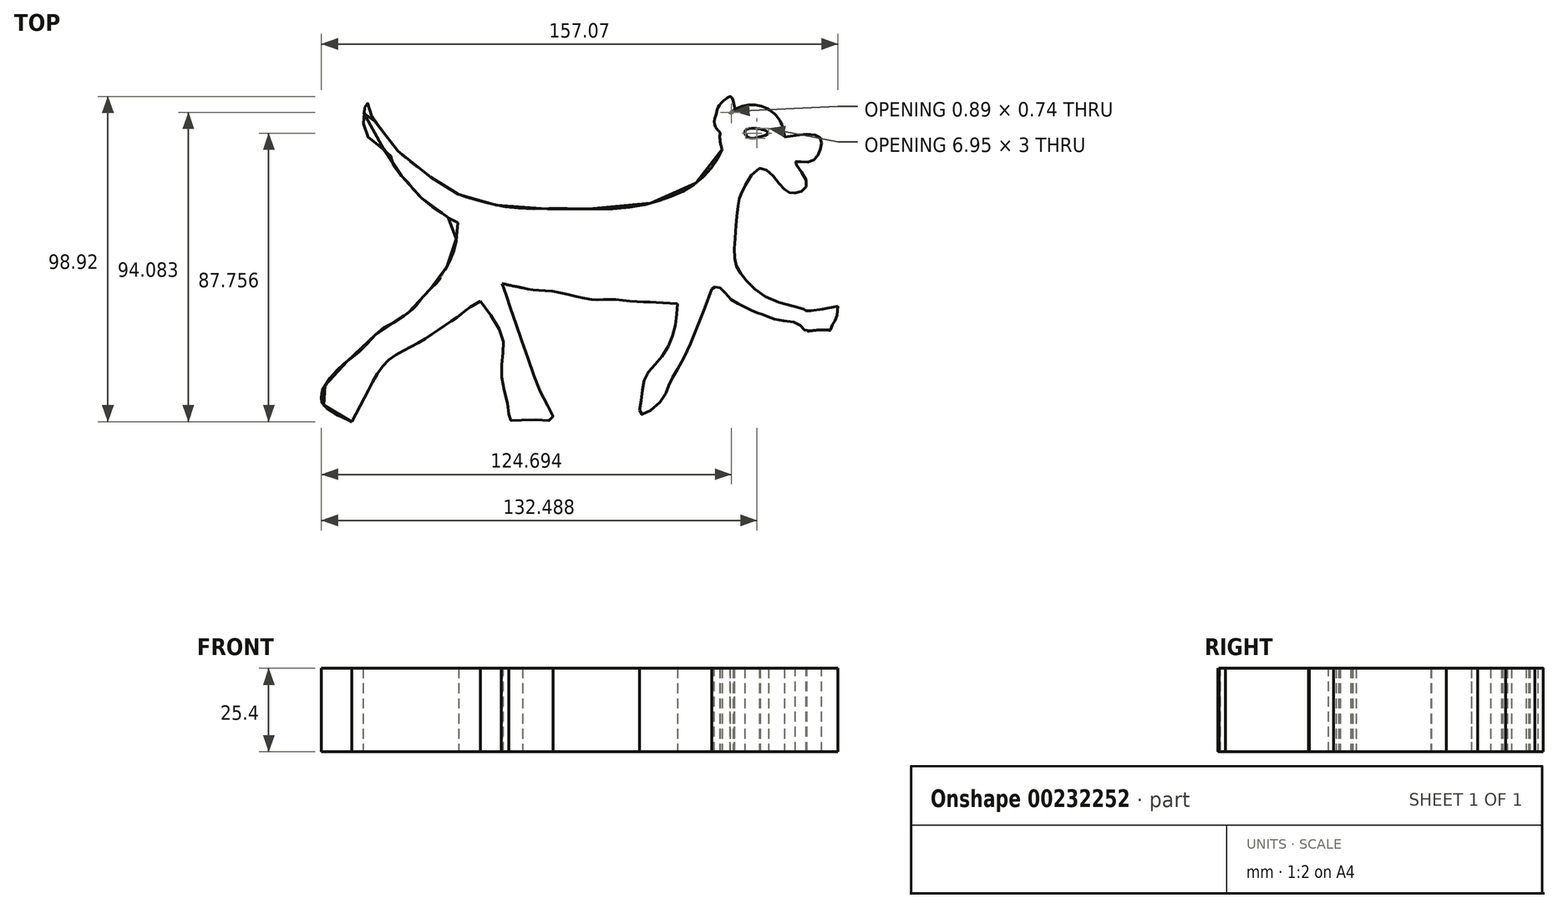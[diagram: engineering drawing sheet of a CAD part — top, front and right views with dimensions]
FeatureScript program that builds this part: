
annotation { "Feature Type Name" : "Feature", "Feature Type Description" : "" }
export const myFeature = defineFeature(function(context is Context, id is Id, definition is map)
    precondition{}
    {
        {
            var Q0;
            Q0=qCreatedBy(makeId("Top.planeOp"),FACE);
            var sketch = newSketch(context, id + "F0", { "sketchPlane" : qUnion([Q0])});
            skArc(sketch, "E0", {"start": v(29.95, 49.23) * mm, "mid": v(30.03, 49.25) * mm, "end": v(30.11, 49.27) * mm});
            skFitSpline(sketch, "E1", {"points": [v(18.66, 55.01) * mm, v(15.24, 49.3) * mm, v(8.77, 43.53) * mm, v(0, 39.6) * mm, v(-12.93, 37.06) * mm, v(-27.7, 37.06) * mm, v(-31.17, 37.06) * mm, v(-42.72, 37.06) * mm, v(-50.57, 38.22) * mm, v(-54.26, 39.14) * mm, v(-62.35, 41.68) * mm, v(-66.5, 44.45) * mm, v(-68.81, 45.84) * mm, v(-74.58, 49.76) * mm, v(-79.2, 53.69) * mm, v(-85.44, 61.54) * mm, v(-86.13, 62.46) * mm, v(-88.44, 66.16) * mm, v(-89.36, 69.39) * mm, v(-90.52, 64.54) * mm, v(-88.44, 58.07) * mm, v(-82.43, 53.46) * mm, v(-81.28, 50) * mm, v(-78.5, 46.53) * mm, v(-76.2, 43.99) * mm, v(-74.35, 41.68) * mm, v(-69.73, 37.75) * mm, v(-66.27, 35.44) * mm, v(-63.96, 33.83) * mm, v(-61.65, 32.44) * mm, v(-62.11, 29.44) * mm, v(-62.35, 26.44) * mm, v(-63.5, 22.74) * mm, v(-64.89, 19.74) * mm, v(-66.96, 16.05) * mm, v(-68.12, 14.43) * mm, v(-70.89, 11.9) * mm, v(-74.81, 7.04) * mm, v(-75.5, 6.35) * mm, v(-80.82, 2.66) * mm, v(-85.44, 0) * mm, v(-90.29, -5.2) * mm, v(-94.44, -8.66) * mm, v(-97.21, -10.97) * mm, v(-100.9, -14.9) * mm, v(-102.52, -17.43) * mm, v(-103.22, -19.05) * mm, v(-103.22, -21.13) * mm, v(-102.99, -22.28) * mm, v(-98.6, -25.75) * mm, v(-94.44, -27.6) * mm, v(-93.98, -27.82) * mm], "startDerivative": vector(-125.96, -246.77) * mm, "endDerivative": vector(52.68, -30.16) * mm});
            skFitSpline(sketch, "E2", {"points": [v(37.5, 58.77) * mm, v(48.26, 58.77) * mm, v(48.26, 54.38) * mm, v(44.8, 51.15) * mm, v(40.87, 51.15) * mm, v(44.33, 44.68) * mm, v(40.64, 41.68) * mm, v(36.71, 43.76) * mm, v(30.11, 49.27) * mm, v(24.48, 41.68) * mm, v(23.78, 39.83) * mm, v(22.86, 32.44) * mm, v(22.63, 29.21) * mm, v(22.4, 21.82) * mm, v(24.48, 16.97) * mm, v(33.48, 9.35) * mm, v(44.1, 6.12) * mm, v(44.1, 5.89) * mm, v(53.8, 7.27) * mm], "startDerivative": vector(185.54, 29.68) * mm, "endDerivative": vector(199.47, 36.88) * mm});
            skFitSpline(sketch, "E3", {"points": [v(-93.98, -27.82) * mm, v(-89.13, -18.59) * mm, v(-83.36, -9.58) * mm, v(-75.05, -4.5) * mm, v(-67.89, 0) * mm, v(-61.88, 4.04) * mm, v(-58.65, 6.58) * mm, v(-54.96, 8.9) * mm, v(-51.72, 11.43) * mm, v(-48.26, 14.2) * mm], "startDerivative": vector(35.22, 65.88) * mm, "endDerivative": vector(39.36, 30.99) * mm});
            skFitSpline(sketch, "E4", {"points": [v(-43.41, 13.28) * mm, v(-39.25, 12.35) * mm, v(-31.87, 11.66) * mm, v(-21.24, 9.35) * mm, v(-15.24, 9.35) * mm, v(-6.93, 8.66) * mm, v(0, 8.43) * mm, v(9.24, 8.66) * mm, v(15.47, 12.58) * mm, v(16.16, 13.05) * mm, v(17.78, 13.05) * mm, v(20.78, 9.81) * mm, v(24.48, 7.5) * mm, v(27.94, 5.89) * mm, v(30.25, 4.96) * mm, v(32.1, 4.27) * mm, v(35.8, 3.12) * mm, v(41.8, 1.96) * mm, v(43.64, 0) * mm, v(47.1, 0) * mm, v(51.03, 0) * mm, v(51.5, 0) * mm, v(52.42, 2.2) * mm, v(53.1, 3.12) * mm, v(53.8, 7.27) * mm], "startDerivative": vector(91.81, -25.71) * mm, "endDerivative": vector(11.2, 121.27) * mm});
            skFitSpline(sketch, "E5", {"points": [v(-48.26, 14.2) * mm, v(-42.1, 12.91) * mm, v(-43.41, 13.28) * mm, v(-48.26, 14.2) * mm]});
            skArc(sketch, "E6.trimOffspring", {"start": v(37.5, 58.77) * mm, "mid": v(31.59, 67.77) * mm, "end": v(20.98, 65.9) * mm});
            skFitSpline(sketch, "E7", {"points": [v(32.7, 59.95) * mm, v(31.73, 60.74) * mm, v(29.74, 61.31) * mm, v(27.7, 61.43) * mm, v(25.57, 60.64) * mm, v(26.43, 58.77) * mm, v(29.85, 58.77) * mm, v(32.7, 59.95) * mm]});
            skFitSpline(sketch, "E8", {"points": [v(20.16, 58.3) * mm, v(16.28, 62.66) * mm, v(16.88, 65.92) * mm, v(17.41, 67.96) * mm, v(19.6, 70.3) * mm, v(20.25, 70.68) * mm, v(21.3, 71.03) * mm, v(22.35, 66.97) * mm, v(21.87, 66.63) * mm, v(20.98, 65.9) * mm, v(22.58, 64.56) * mm, v(23.39, 64.3) * mm, v(23.76, 63.67) * mm, v(23.97, 63.66) * mm], "startDerivative": vector(-37.5, 29.91) * mm, "endDerivative": vector(7.95, 2.34) * mm});
            skArc(sketch, "E9.trimOffspring", {"start": v(18, 60.12) * mm, "mid": v(17.99, 57.52) * mm, "end": v(18.66, 55.01) * mm});
            skFitSpline(sketch, "E10", {"points": [v(-48.26, 14.2) * mm, v(-45.63, 6.35) * mm, v(-40.55, -8.2) * mm, v(-35.24, -21.6) * mm, v(-32.93, -27.13) * mm, v(-39.63, -27.13) * mm, v(-45.86, -27.36) * mm, v(-46.32, -24.13) * mm, v(-48.26, -16.05) * mm, v(-48.26, -8.43) * mm, v(-48.26, -1.96) * mm, v(-54.96, 8.9) * mm], "startDerivative": vector(26.13, -79.42) * mm, "endDerivative": vector(-77.14, 101.6) * mm});
            skFitSpline(sketch, "E11", {"points": [v(15.47, 12.58) * mm, v(6.32, -9.58) * mm, v(2.63, -16.05) * mm, v(0, -21.6) * mm, v(-6.15, -25.52) * mm, v(-5.91, -21.13) * mm, v(-4.76, -14.2) * mm, v(0, -8.43) * mm, v(4.01, 0) * mm, v(4.98, 8.07) * mm], "startDerivative": vector(-51.55, -137.28) * mm, "endDerivative": vector(3.75, 73.8) * mm});
            skSolve(sketch);
        }
        {
            var Q0;
            Q0 = qSketchRegion(id + "F0", true);
            extrude(context, id + "F1", {"entities" : qUnion([Q0]), "depth" : 25.4 * mm});
        }
        {
            var Q0;
            Q0 = qSketchRegion(id + "F0", true);
            extrude(context, id + "F2", {"entities" : qUnion([Q0]), "operationType" : NewBodyOperationType.ADD, "depth" : 25.4 * mm});
        }
    });
